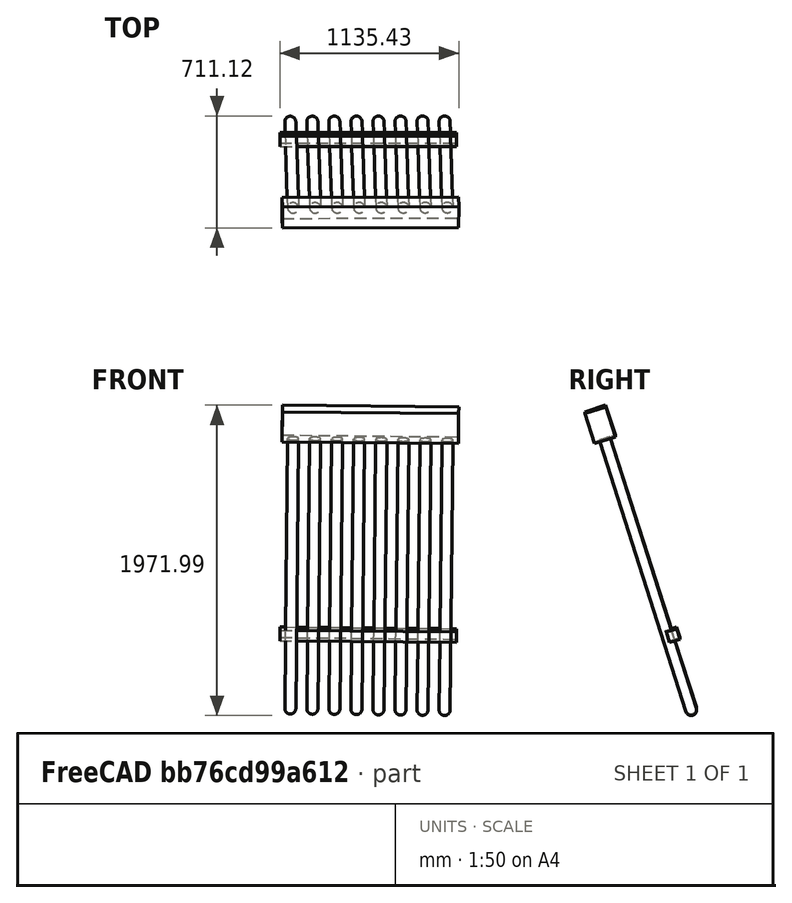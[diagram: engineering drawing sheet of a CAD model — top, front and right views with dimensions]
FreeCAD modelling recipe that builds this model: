
FCSTD DOCUMENT  (FreeCAD 0.19R23578 (Git))
Label: SolarTube
License: Creative Commons Attribution-ShareAlike
LicenseURL: http://creativecommons.org/licenses/by-sa/4.0/
objects: Part::FeaturePython×5, Part::Box×2, Part::Sphere×1, Part::Cylinder×1, Part::MultiFuse×1, App::MaterialObjectPython×1, App::DocumentObjectGroupPython×1, App::GeometryPython×1
note: 11 computed .brp shape members not serialized (recipe doc carries the construction recipe); baked Part::Feature solids carry a one-line shape summary decoded from their .brp

FEATURE [Part::Sphere] Sphere
  Angle1 = -90
  Angle2 = 90
  Angle3 = 360
  AttacherType = Attacher::AttachEngine3D
  Radius = 35
FEATURE [Part::Cylinder] Cylinder
  Angle = 360
  AttacherType = Attacher::AttachEngine3D
  Height = 1800
  Radius = 35
FEATURE [Part::MultiFuse] Fusion
  Refine = true
  Shapes = -> [Sphere,Cylinder]
FEATURE [Part::Box] Box  label="Cube"
  AttacherType = Attacher::AttachEngine3D
  Height = 200
  Length = 1120
  Placement = pos=(-70,-70,1800) rot=(0,0,1;0rad)
  Width = 140
  expr: Length = Width * <<Array>>.NumberX
  expr: .Placement.Base.x = -Width / 2
  expr: .Placement.Base.y = -Width / 2
  expr: .Placement.Base.z = <<Cylinder>>.Height
  expr: Width = <<Sphere>>.Radius * 4
FEATURE [Part::FeaturePython] Component  label="Tube"  # Arch/BIM 0 (typed FeaturePython)
  Base = -> Fusion
  HorizontalArea = 0
  IfcData = attributes={"GlobalId": {"name": "GlobalId", "type": "IfcGloballyUniqueId", "is_enum": false, "enum_values": []}, "Description": {"... (+538 chars omitted),+1 more (map truncated)
  IfcType = 0
  MoveBase = true
  MoveWithHost = true
  PerimeterLength = 0
  PredefinedType = 0
  VerticalArea = 0
FEATURE [Part::FeaturePython] Array  # Draft array (typed FeaturePython)
  Angle = 360
  ArrayType = 0
  Axis = (0,0,1)
  Base = -> Component
  Center = (0,0,0)
  Fuse = false
  IntervalAxis = (0,0,0)
  IntervalX = (140,0,0)
  IntervalY = (0,1,0)
  IntervalZ = (0,0,50)
  NumberCircles = 3
  NumberPolar = 5
  NumberX = 8
  NumberY = 1
  NumberZ = 1
  RadialDistance = 50
  Symmetry = 1
  TangentialDistance = 25
  expr: .IntervalX.x = <<Cylinder>>.Radius * 4
FEATURE [Part::Box] Box001  label="TubeSupport"
  AttacherType = Attacher::AttachEngine3D
  Height = 70
  Length = 1120
  Placement = pos=(-70,0,450) rot=(0,0,1;0rad)
  Width = 70
  expr: .Placement.Base.z = <<Cylinder>>.Height / 4
  expr: Length = Width * 2 * <<Array>>.NumberX
  expr: .Placement.Base.x = -Width
  expr: Width = <<Sphere>>.Radius * 2
FEATURE [Part::FeaturePython] Component001  label="Manifold"  # Arch/BIM 0 (typed FeaturePython)
  Base = -> Box
  HorizontalArea = 0
  IfcData = attributes={"GlobalId": {"name": "GlobalId", "type": "IfcGloballyUniqueId", "is_enum": false, "enum_values": []}, "Description": {"... (+532 chars omitted),+1 more (map truncated)
  IfcType = 0
  MoveBase = true
  MoveWithHost = true
  PerimeterLength = 0
  Placement = pos=(-52.2425,-613.83,1694.19) rot=(0.999467,0.032635,0;0.308961rad)
  PredefinedType = 6
  VerticalArea = 0
FEATURE [Part::FeaturePython] Component002  label="Support"  # Arch/BIM 0 (typed FeaturePython)
  Base = -> Box001
  HorizontalArea = 0
  IfcData = attributes={"GlobalId": {"name": "GlobalId", "type": "IfcGloballyUniqueId", "is_enum": false, "enum_values": []}, "Description": {"... (+532 chars omitted),+1 more (map truncated)
  IfcType = 0
  MoveBase = true
  MoveWithHost = true
  PerimeterLength = 0
  Placement = pos=(-65.5309,-136.866,429.387) rot=(0.999467,0.032635,0;0.308961rad)
  PredefinedType = 6
  VerticalArea = 0
FEATURE [App::MaterialObjectPython] Material  label="Glass"  # material (typed FeaturePython)
  Description = Generic soda-lime glass
  Material = AuthorAndLicense=Glass-Generic,CardName=Glass-Generic,Color=(0.0, 0.3333333333333333, 1.0, 1.0),Density=2520 kg/m^3,+13 more (map truncated)
  ProductURL = https://en.wikipedia.org/wiki/Soda-lime_glass
  Transparency = 80
FEATURE [Part::FeaturePython] Component003  label="Tubes"  # Arch/BIM 11 (typed FeaturePython)
  Base = -> Array
  HorizontalArea = 0
  IfcData = attributes={"GlobalId": {"name": "GlobalId", "type": "IfcGloballyUniqueId", "is_enum": false, "enum_values": []}, "Description": {"... (+538 chars omitted),+1 more (map truncated)
  IfcType = 11
  Material = -> Material
  MoveBase = true
  MoveWithHost = true
  PerimeterLength = 0
  Placement = pos=(0,0,0) rot=(0.999467,0.032635,0;0.308961rad)
  VerticalArea = 0
FEATURE [App::DocumentObjectGroupPython] MaterialContainer  label="Materials"  # scripted group (container) (typed FeaturePython)
  Group = -> [Material]
FEATURE [App::GeometryPython] BuildingPart  label="SolarTubeArray"  # Arch/BIM 172 (typed FeaturePython)
  Area = 0
  Group = -> [Component001,Component002,Component003,MaterialContainer]
  Height = 0
  HeightPropagate = true
  IfcData = attributes={"GlobalId": {"name": "GlobalId", "type": "IfcGloballyUniqueId", "is_enum": false, "enum_values": []}, "Description": {"... (+484 chars omitted),+1 more (map truncated)
  IfcType = 172
  LevelOffset = 0
  Placement = pos=(0,0,0) rot=(0.994421,0.016231,0.104231;0.310667rad)
  PredefinedType = 0
